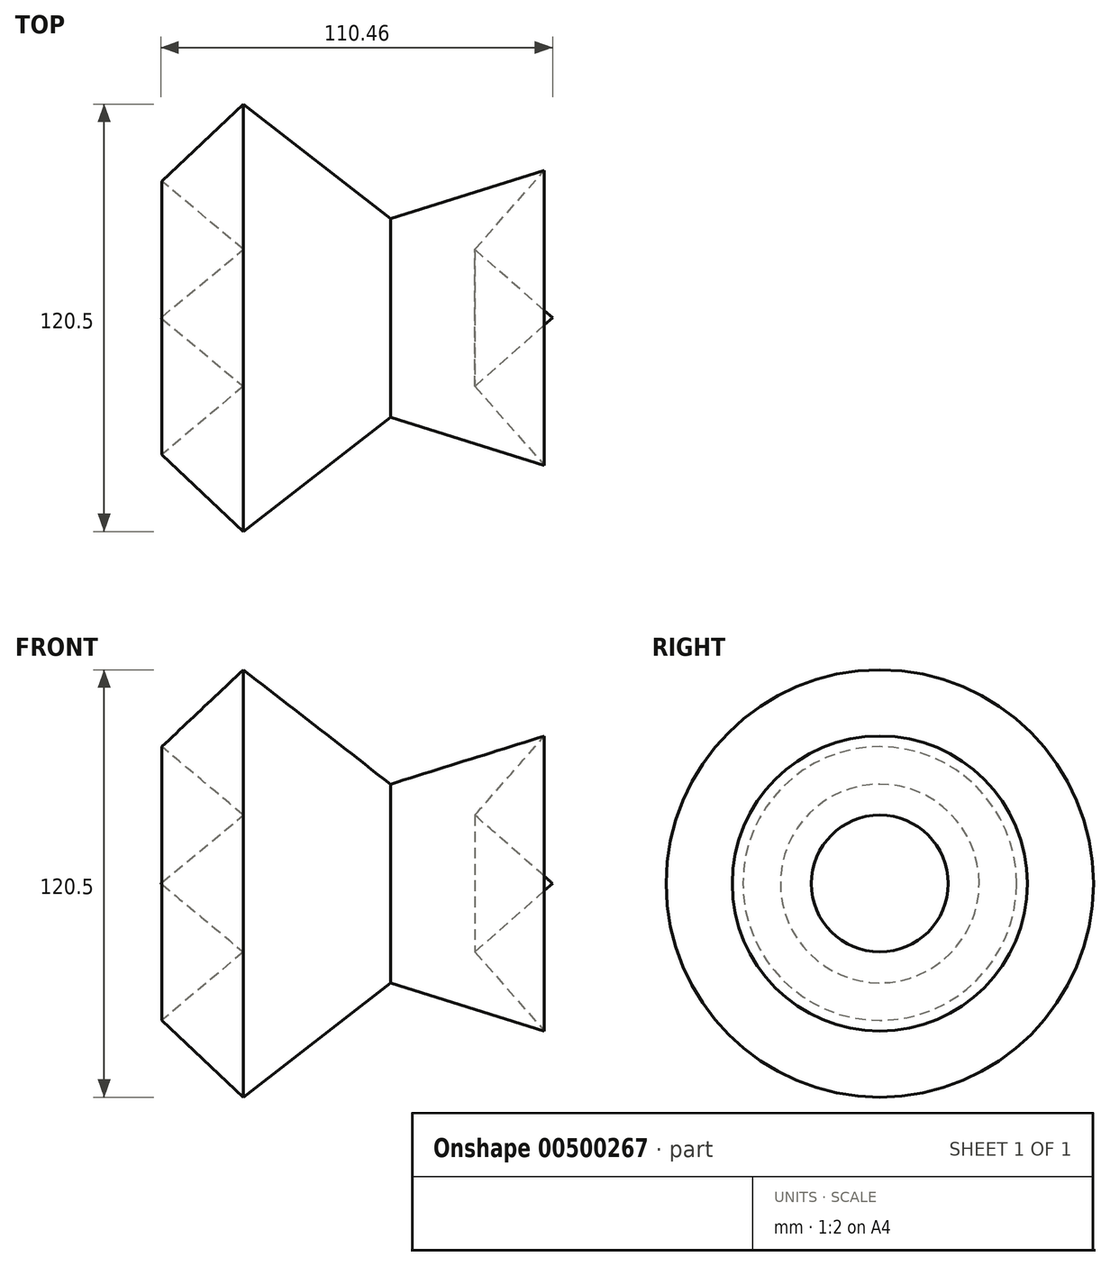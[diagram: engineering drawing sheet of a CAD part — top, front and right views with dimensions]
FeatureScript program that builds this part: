
annotation { "Feature Type Name" : "Feature", "Feature Type Description" : "" }
export const myFeature = defineFeature(function(context is Context, id is Id, definition is map)
    precondition{}
    {
        {
            var Q0;
            Q0=qCreatedBy(makeId("Top.planeOp"),FACE);
            var sketch = newSketch(context, id + "F0", { "sketchPlane" : qUnion([Q0])});
            skLineSegment(sketch, "E0", {"start": v(-41.49, 0) * mm, "end": v(-64.74, -19.3) * mm});
            skLineSegment(sketch, "E1", {"start": v(-41.49, 0) * mm, "end": v(-64.48, 19.3) * mm});
            skLineSegment(sketch, "E2", {"start": v(-64.74, -19.3) * mm, "end": v(45.72, -19.3) * mm});
            skLineSegment(sketch, "E3", {"start": v(45.72, -19.3) * mm, "end": v(23.78, 0) * mm});
            skLineSegment(sketch, "E4", {"start": v(23.78, 0) * mm, "end": v(43.4, 22.3) * mm});
            skLineSegment(sketch, "E5", {"start": v(43.4, 22.3) * mm, "end": v(0, 8.72) * mm});
            skLineSegment(sketch, "E6", {"start": v(0, 8.72) * mm, "end": v(-41.49, 40.96) * mm});
            skLineSegment(sketch, "E7", {"start": v(-41.49, 40.96) * mm, "end": v(-64.48, 19.3) * mm});
            skSolve(sketch);
        }
        {
            var Q0;
            Q0=makeQuery(id+"F0.imprint","IMPRINT",FACE,{"disambiguationData":[TD([[makeQuery(id+"F0.imprint","IMPRINT",EDGE,{"derivedFrom":sQuery(id+"F0.wireOp",EDGE,"E0")}),1.0]])]});
            var Q1;
            Q1=sQuery(id+"F0.wireOp",EDGE,"E2");
            revolve(context, id + "F1", {"entities" : qUnion([Q0]), "axis" : qUnion([Q1]), "revolveType" : RevolveType.FULL});
        }
    });
